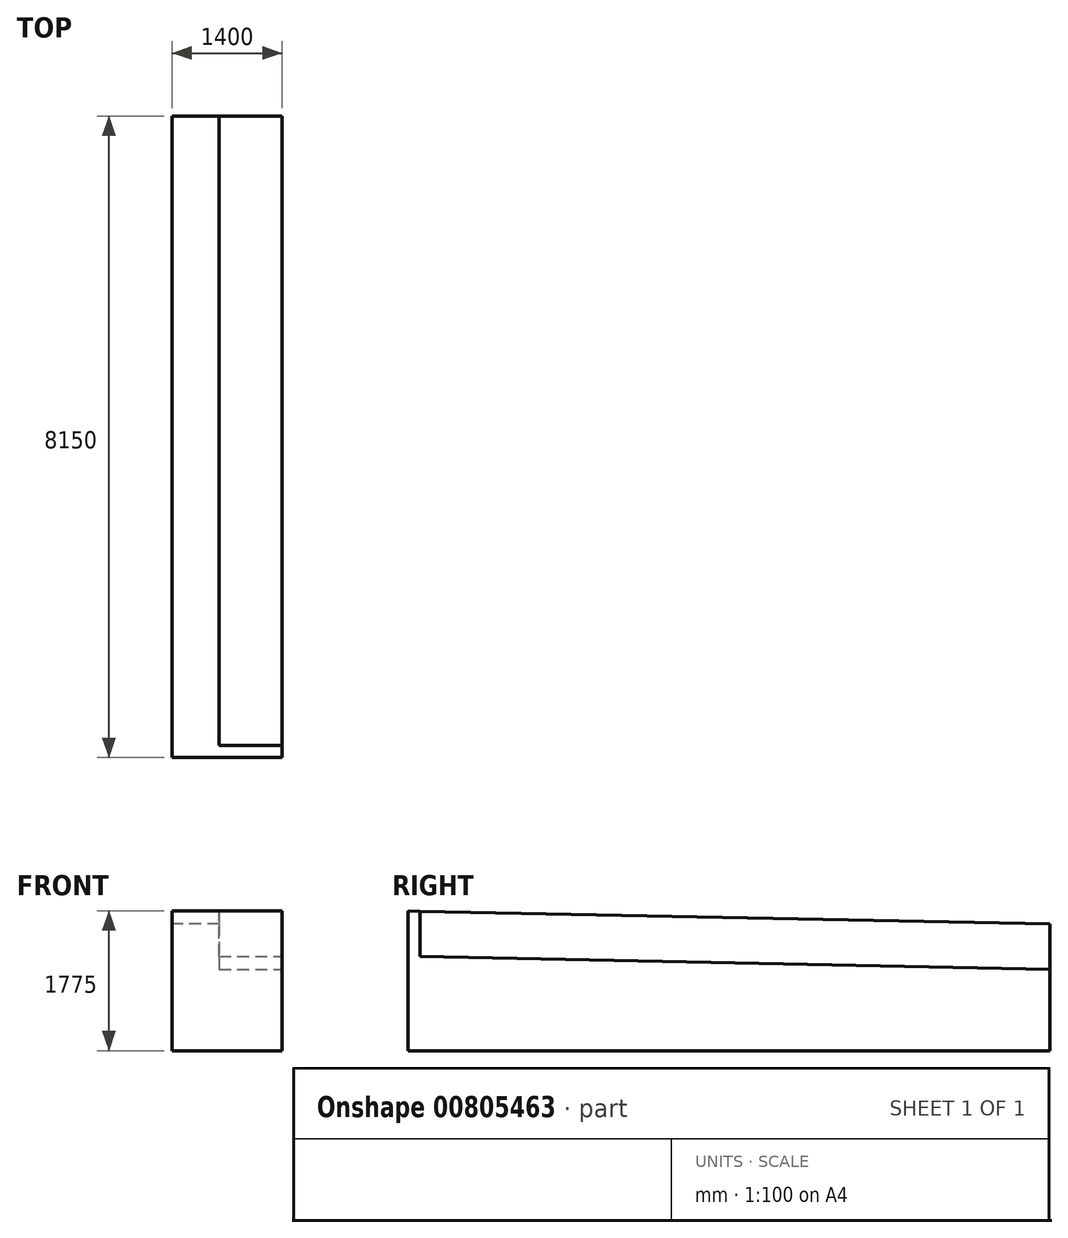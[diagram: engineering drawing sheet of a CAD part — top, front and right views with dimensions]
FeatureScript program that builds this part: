
annotation { "Feature Type Name" : "Feature", "Feature Type Description" : "" }
export const myFeature = defineFeature(function(context is Context, id is Id, definition is map)
    precondition{}
    {
        {
            var Q0;
            Q0=qCreatedBy(makeId("Right.planeOp"),FACE);
            var sketch = newSketch(context, id + "F0", { "sketchPlane" : qUnion([Q0])});
            skLineSegment(sketch, "E0", {"start": v(8150, 0) * mm, "end": v(0, 0) * mm});
            skLineSegment(sketch, "E1", {"start": v(0, 0) * mm, "end": v(0, 1775) * mm});
            skLineSegment(sketch, "E2", {"start": v(0, 1775) * mm, "end": v(8150, 1610) * mm});
            skLineSegment(sketch, "E3", {"start": v(8150, 1610) * mm, "end": v(8150, 0) * mm});
            skSolve(sketch);
        }
        {
            var Q0;
            Q0 = qSketchRegion(id + "F0", true);
            extrude(context, id + "F1", {"entities" : qUnion([Q0]), "depth" : 1400 * mm, "offsetDistance" : 25 * mm});
        }
        {
            var Q0;
            Q0=makeQuery(id+"F1.opExtrude","CAP_FACE",FACE,{"disambiguationData":[OSD([sQuery(id+"F0.wireOp",EDGE,"E0"),sQuery(id+"F0.wireOp",EDGE,"E1"),sQuery(id+"F0.wireOp",EDGE,"E2"),sQuery(id+"F0.wireOp",EDGE,"E3")])],"isStart":false});
            var sketch = newSketch(context, id + "F2", { "sketchPlane" : qUnion([Q0])});
            skLineSegment(sketch, "E4", {"start": v(8150, 1610) * mm, "end": v(8150, 1035) * mm});
            skLineSegment(sketch, "E5", {"start": v(150, 1195) * mm, "end": v(150, 1771.96) * mm});
            skLineSegment(sketch, "E6", {"start": v(150, 1771.96) * mm, "end": v(8150, 1610) * mm});
            skLineSegment(sketch, "E7", {"start": v(150, 1195) * mm, "end": v(8150, 1035) * mm});
            skSolve(sketch);
        }
        {
            var Q0;
            Q0 = qSketchRegion(id + "F2", true);
            extrude(context, id + "F3", {"entities" : qUnion([Q0]), "operationType" : NewBodyOperationType.REMOVE, "oppositeDirection" : true, "depth" : 800 * mm, "offsetDistance" : 25 * mm});
        }
    });
